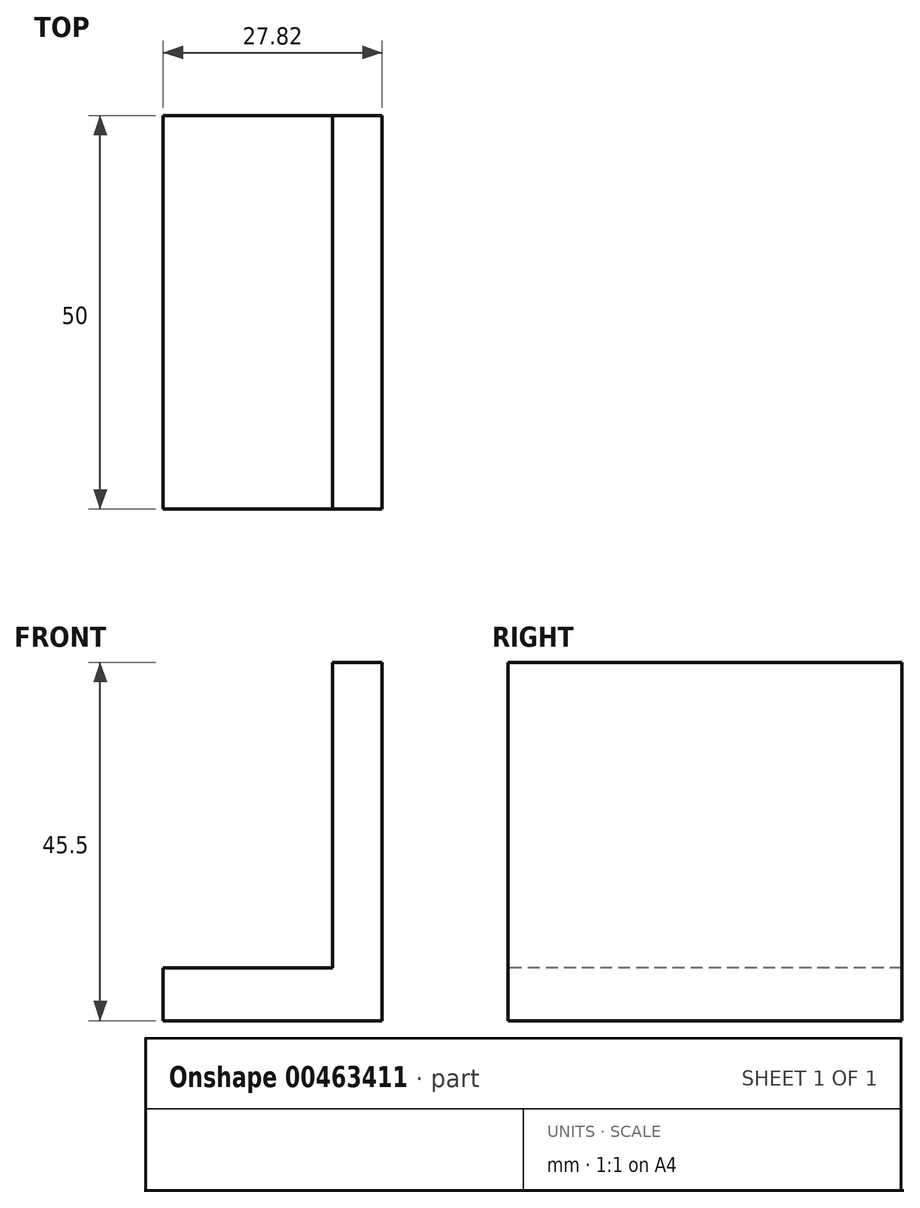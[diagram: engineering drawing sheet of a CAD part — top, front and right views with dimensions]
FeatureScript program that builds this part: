
annotation { "Feature Type Name" : "Feature", "Feature Type Description" : "" }
export const myFeature = defineFeature(function(context is Context, id is Id, definition is map)
    precondition{}
    {
        {
            var Q0;
            Q0=qCreatedBy(makeId("Front.planeOp"),FACE);
            var sketch = newSketch(context, id + "F0", { "sketchPlane" : qUnion([Q0])});
            skLineSegment(sketch, "E0", {"start": v(-58.74, 0) * mm, "end": v(-58.74, 38.8) * mm});
            skLineSegment(sketch, "E1", {"start": v(-58.74, 38.8) * mm, "end": v(-52.46, 38.8) * mm});
            skLineSegment(sketch, "E2", {"start": v(-52.46, 38.8) * mm, "end": v(-52.46, 0) * mm});
            skLineSegment(sketch, "E3", {"start": v(-52.46, 0) * mm, "end": v(-52.46, -6.7) * mm});
            skLineSegment(sketch, "E4", {"start": v(-52.46, -6.7) * mm, "end": v(-80.28, -6.7) * mm});
            skLineSegment(sketch, "E5", {"start": v(-80.28, -6.7) * mm, "end": v(-80.28, 0) * mm});
            skLineSegment(sketch, "E6", {"start": v(-80.28, 0) * mm, "end": v(-58.74, 0) * mm});
            skSolve(sketch);
        }
        {
            var Q0;
            Q0=qSketchRegion(id+"F0",true);
            extrude(context, id + "F1", {"entities" : qUnion([Q0]), "oppositeDirection" : true, "depth" : 50 * mm, "offsetDistance" : 25 * mm});
        }
    });
